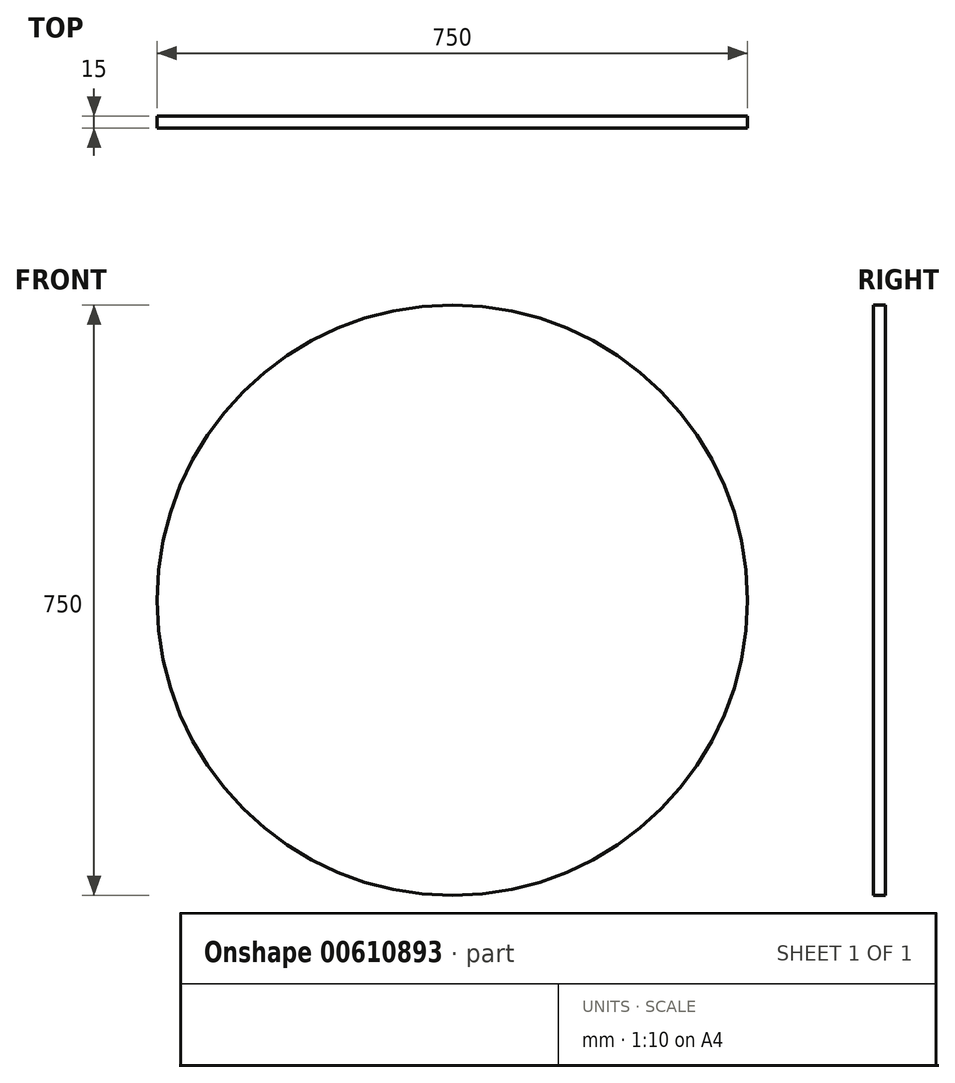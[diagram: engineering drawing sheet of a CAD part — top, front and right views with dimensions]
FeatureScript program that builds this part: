
annotation { "Feature Type Name" : "Feature", "Feature Type Description" : "" }
export const myFeature = defineFeature(function(context is Context, id is Id, definition is map)
    precondition{}
    {
        {
            var Q0;
            Q0=qCreatedBy(makeId("Front.planeOp"),FACE);
            var sketch = newSketch(context, id + "F0", { "sketchPlane" : qUnion([Q0])});
            skCircle(sketch, "E0", {"center": v(0, 0) * mm, "radius": 375 * mm});
            skSolve(sketch);
        }
        {
            var Q0;
            Q0=makeQuery(id+"F0.imprint","IMPRINT",FACE,{"disambiguationData":[TD([[makeQuery(id+"F0.imprint","IMPRINT",EDGE,{"derivedFrom":sQuery(id+"F0.wireOp",EDGE,"E0")}),1.0]])]});
            extrude(context, id + "F1", {"entities" : qUnion([Q0]), "depth" : 15 * mm, "offsetDistance" : 25 * mm});
        }
    });
